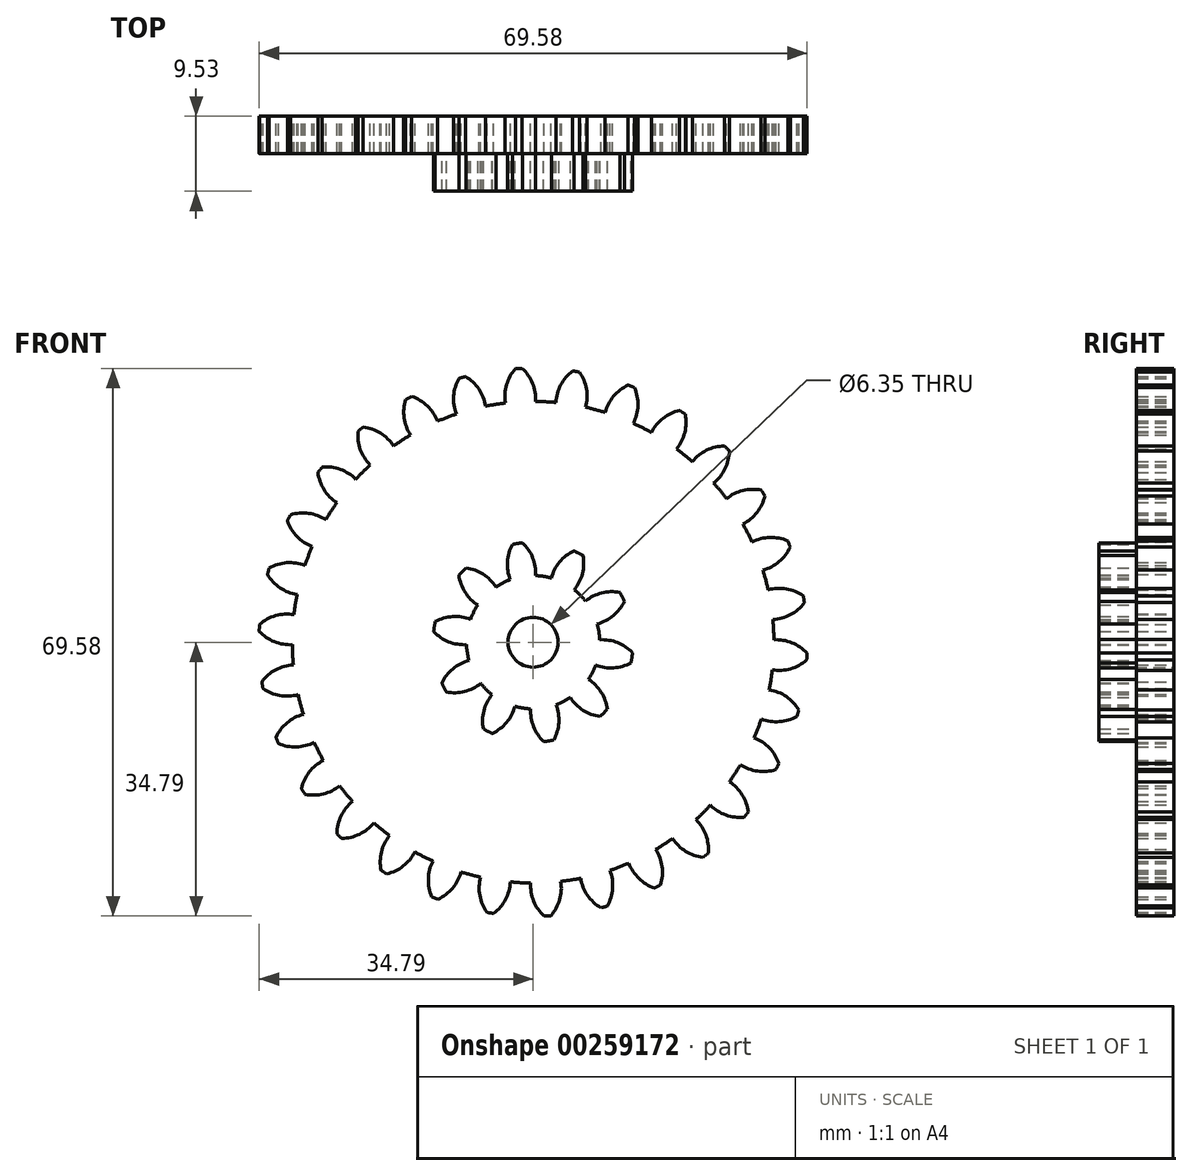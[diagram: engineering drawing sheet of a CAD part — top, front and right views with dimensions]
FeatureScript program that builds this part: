
annotation { "Feature Type Name" : "Feature", "Feature Type Description" : "" }
export const myFeature = defineFeature(function(context is Context, id is Id, definition is map)
    precondition{}
    {
        {
            var Q0;
            Q0=qCreatedBy(makeId("Front.planeOp"),FACE);
            var sketch = newSketch(context, id + "F0", { "sketchPlane" : qUnion([Q0])});
            skCircle(sketch, "E0", {"center": v(0, 0) * mm, "radius": 30.59 * mm});
            skCircle(sketch, "E1", {"center": v(0, 0) * mm, "radius": 32.7 * mm, "construction": true});
            skCircle(sketch, "E2", {"center": v(0, 0) * mm, "radius": 34.82 * mm, "construction": true});
            skLineSegment(sketch, "E3", {"start": v(0, 34.82) * mm, "end": v(0, 0) * mm, "construction": true});
            skLineSegment(sketch, "E4", {"start": v(0, 0) * mm, "end": v(-1.82, 34.77) * mm, "construction": true});
            skLineSegment(sketch, "E5", {"start": v(0, 32.7) * mm, "end": v(-37.65, 32.7) * mm, "construction": true});
            skLineSegment(sketch, "E6", {"start": v(0, 32.7) * mm, "end": v(-35.97, 19.61) * mm, "construction": true});
            skArc(sketch, "E7", {"start": v(0.31, 30.59) * mm, "mid": v(-0.07, 32.88) * mm, "end": v(-1.4, 34.8) * mm});
            skArc(sketch, "E8.MirrorCS", {"start": v(-3.5, 30.39) * mm, "mid": v(-3.37, 32.7) * mm, "end": v(-2.25, 34.75) * mm});
            skArc(sketch, "E9", {"start": v(-1.4, 34.8) * mm, "mid": v(-1.82, 34.77) * mm, "end": v(-2.25, 34.75) * mm});
            skCircle(sketch, "E10", {"center": v(0, 0) * mm, "radius": 3.18 * mm});
            skSolve(sketch);
        }
        {
            var Q0;
            Q0 = qSketchRegion(id + "F0", true);
            extrude(context, id + "F1", {"entities" : qUnion([Q0]), "depth" : 4.76 * mm});
        }
        {
            var Q0;
            Q0=makeQuery(id+"F1.opExtrude","CAP_FACE",FACE,{"disambiguationData":[OSD([sQuery(id+"F0.wireOp",EDGE,"E0"),sQuery(id+"F0.wireOp",EDGE,"E7"),sQuery(id+"F0.wireOp",EDGE,"E8.MirrorCS"),sQuery(id+"F0.wireOp",EDGE,"E9"),sQuery(id+"F0.wireOp",EDGE,"E10")])],"isStart":false});
            var sketch = newSketch(context, id + "F2", { "sketchPlane" : qUnion([Q0])});
            skCircle(sketch, "E11", {"center": v(0, 0) * mm, "radius": 3.18 * mm});
            skCircle(sketch, "E12", {"center": v(0, 0) * mm, "radius": 8.47 * mm});
            skCircle(sketch, "E13", {"center": v(0, 0) * mm, "radius": 10.58 * mm, "construction": true});
            skCircle(sketch, "E14", {"center": v(0, 0) * mm, "radius": 12.7 * mm, "construction": true});
            skLineSegment(sketch, "E15", {"start": v(0, 12.7) * mm, "end": v(0, 0) * mm, "construction": true});
            skLineSegment(sketch, "E16", {"start": v(0, 0) * mm, "end": v(-1.99, 12.54) * mm, "construction": true});
            skLineSegment(sketch, "E17", {"start": v(0, 10.58) * mm, "end": v(-15.06, 10.58) * mm, "construction": true});
            skLineSegment(sketch, "E18", {"start": v(0, 10.58) * mm, "end": v(-14.53, 5.3) * mm, "construction": true});
            skArc(sketch, "E19", {"start": v(0.3, 8.46) * mm, "mid": v(-0.06, 10.73) * mm, "end": v(-1.35, 12.63) * mm});
            skArc(sketch, "E20.MirrorCS", {"start": v(-2.9, 7.95) * mm, "mid": v(-3.26, 10.22) * mm, "end": v(-2.62, 12.43) * mm});
            skArc(sketch, "E21", {"start": v(-1.35, 12.63) * mm, "mid": v(-1.99, 12.54) * mm, "end": v(-2.62, 12.43) * mm});
            skSolve(sketch);
        }
        {
            var Q0;
            Q0 = qSketchRegion(id + "F2", true);
            extrude(context, id + "F3", {"entities" : qUnion([Q0]), "operationType" : NewBodyOperationType.ADD, "depth" : 4.76 * mm});
        }
        {
            var Q0;
            Q0=makeQuery(id+"F1.opExtrude","SWEPT_FACE",FACE,{"disambiguationData":[OSD([sQuery(id+"F0.wireOp",EDGE,"E7")])]});
            var Q1;
            Q1=makeQuery(id+"F1.opExtrude","SWEPT_FACE",FACE,{"disambiguationData":[OSD([sQuery(id+"F0.wireOp",EDGE,"E8.MirrorCS")])]});
            var Q2;
            Q2=makeQuery(id+"F1.opExtrude","SWEPT_FACE",FACE,{"disambiguationData":[OSD([sQuery(id+"F0.wireOp",EDGE,"E9")])]});
            var Q3;
            Q3=makeQuery(id+"F1.opExtrude","SWEPT_FACE",FACE,{"disambiguationData":[OSD([sQuery(id+"F0.wireOp",EDGE,"E0")])]});
            circularPattern(context, id + "F4", {"patternType" : PatternType.FACE, "faces" : qUnion([Q0, Q1, Q2]), "axis" : qUnion([Q3]), "angle" : 360 * degree, "instanceCount" : 30, "equalSpace" : true});
        }
        {
            var Q0;
            Q0=makeQuery(id+"F3.opExtrude","SWEPT_FACE",FACE,{"disambiguationData":[OSD([sQuery(id+"F2.wireOp",EDGE,"E19")])]});
            var Q1;
            Q1=makeQuery(id+"F3.opExtrude","SWEPT_FACE",FACE,{"disambiguationData":[OSD([sQuery(id+"F2.wireOp",EDGE,"E21")])]});
            var Q2;
            Q2=makeQuery(id+"F3.opExtrude","SWEPT_FACE",FACE,{"disambiguationData":[OSD([sQuery(id+"F2.wireOp",EDGE,"E20.MirrorCS")])]});
            var Q3;
            Q3=makeQuery(id+"F3.opExtrude","SWEPT_FACE",FACE,{"disambiguationData":[OSD([sQuery(id+"F2.wireOp",EDGE,"E12")])]});
            circularPattern(context, id + "F5", {"patternType" : PatternType.FACE, "faces" : qUnion([Q0, Q1, Q2]), "axis" : qUnion([Q3]), "angle" : 360 * degree, "instanceCount" : 10, "equalSpace" : true});
        }
    });
